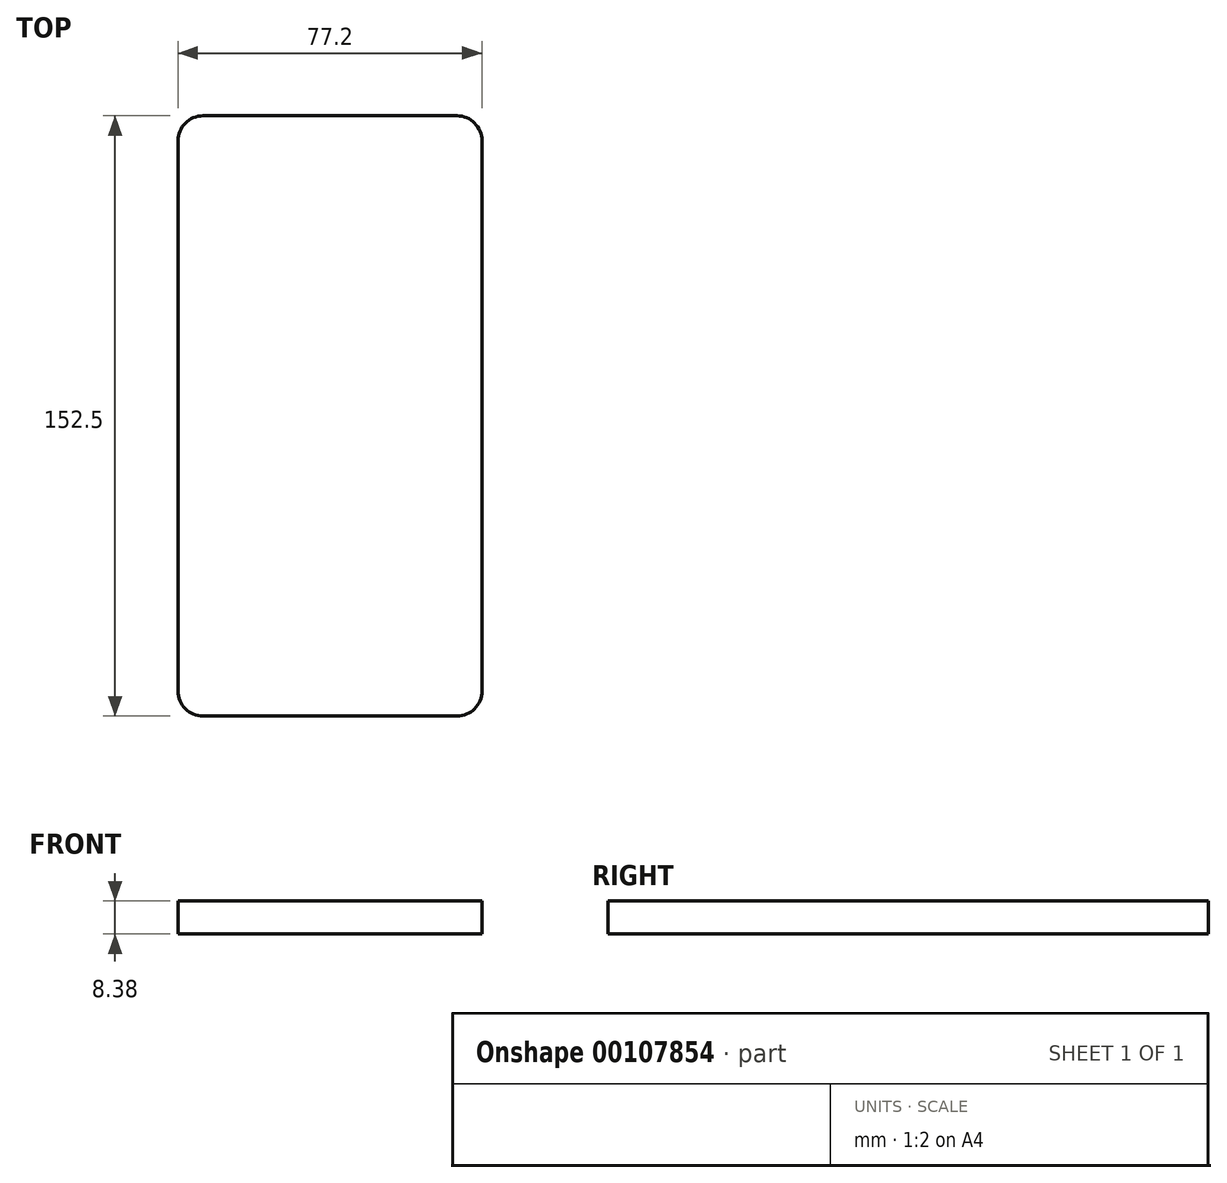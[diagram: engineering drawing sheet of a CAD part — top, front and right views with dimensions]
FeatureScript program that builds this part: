
annotation { "Feature Type Name" : "Feature", "Feature Type Description" : "" }
export const myFeature = defineFeature(function(context is Context, id is Id, definition is map)
    precondition{}
    {
        {
            var Q0;
            Q0=qCreatedBy(makeId("Top.planeOp"),FACE);
            var sketch = newSketch(context, id + "F0", { "sketchPlane" : qUnion([Q0])});
            skLineSegment(sketch, "E0.bottom", {"start": v(-27.68, 110.74) * mm, "end": v(36.82, 110.74) * mm});
            skLineSegment(sketch, "E0.top", {"start": v(-27.68, -41.76) * mm, "end": v(36.82, -41.76) * mm});
            skLineSegment(sketch, "E0.left", {"start": v(-34.03, 104.4) * mm, "end": v(-34.03, -35.4) * mm});
            skLineSegment(sketch, "E0.right", {"start": v(43.17, 104.4) * mm, "end": v(43.17, -35.4) * mm});
            skPoint(sketch, "E1.visualSharp", {"position": v(-34.03, 110.74) * mm});
            skArc(sketch, "E1.filletArc", {"start": v(-27.68, 110.74) * mm, "mid": v(-32.17, 108.88) * mm, "end": v(-34.03, 104.4) * mm});
            skPoint(sketch, "E2.visualSharp", {"position": v(43.17, 110.74) * mm});
            skArc(sketch, "E2.filletArc", {"start": v(43.17, 104.4) * mm, "mid": v(41.3, 108.88) * mm, "end": v(36.82, 110.74) * mm});
            skPoint(sketch, "E3.visualSharp", {"position": v(-34.03, -41.76) * mm});
            skArc(sketch, "E3.filletArc", {"start": v(-34.03, -35.4) * mm, "mid": v(-32.17, -39.9) * mm, "end": v(-27.68, -41.76) * mm});
            skPoint(sketch, "E4.visualSharp", {"position": v(43.17, -41.76) * mm});
            skArc(sketch, "E4.filletArc", {"start": v(36.82, -41.76) * mm, "mid": v(41.3, -39.9) * mm, "end": v(43.17, -35.4) * mm});
            skSolve(sketch);
        }
        {
            var Q0;
            Q0=makeQuery(id+"F0.imprint","IMPRINT",FACE,{"disambiguationData":[TD([[makeQuery(id+"F0.imprint","IMPRINT",EDGE,{"derivedFrom":sQuery(id+"F0.wireOp",EDGE,"E0.bottom")}),-1.0]])]});
            extrude(context, id + "F1", {"entities" : qUnion([Q0]), "depth" : 8.38 * mm});
        }
    });
